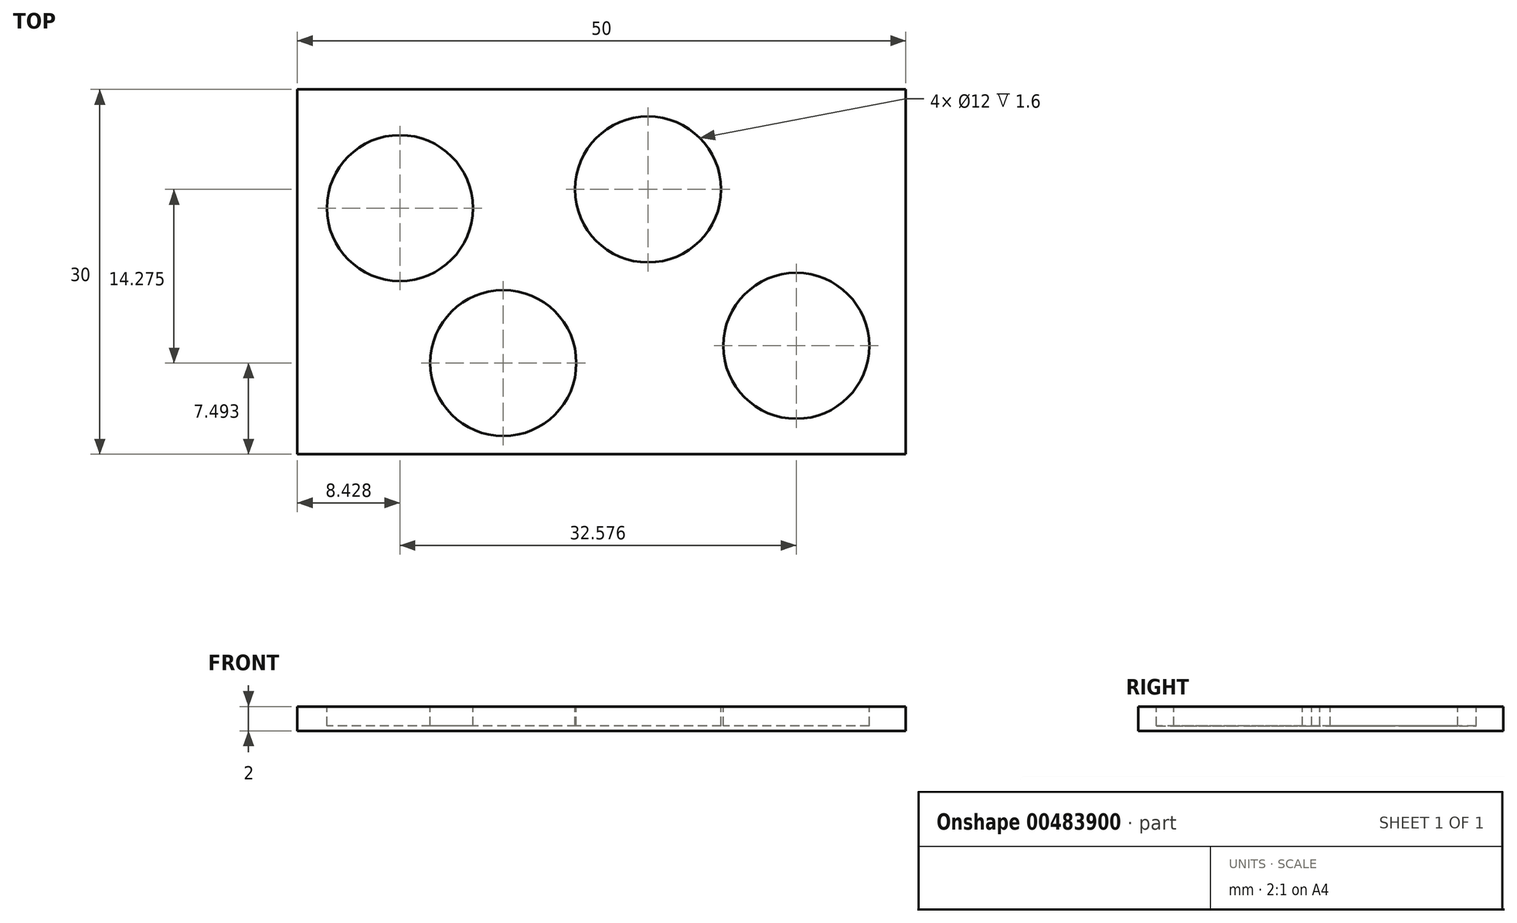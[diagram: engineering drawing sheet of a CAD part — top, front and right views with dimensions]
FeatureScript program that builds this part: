
annotation { "Feature Type Name" : "Feature", "Feature Type Description" : "" }
export const myFeature = defineFeature(function(context is Context, id is Id, definition is map)
    precondition{}
    {
        {
            var Q0;
            Q0=qCreatedBy(makeId("Top.planeOp"),FACE);
            var sketch = newSketch(context, id + "F0", { "sketchPlane" : qUnion([Q0])});
            skLineSegment(sketch, "E0.bottom", {"start": v(-25, 15) * mm, "end": v(25, 15) * mm});
            skLineSegment(sketch, "E0.top", {"start": v(-25, -15) * mm, "end": v(25, -15) * mm});
            skLineSegment(sketch, "E0.left", {"start": v(-25, 15) * mm, "end": v(-25, -15) * mm});
            skLineSegment(sketch, "E0.right", {"start": v(25, 15) * mm, "end": v(25, -15) * mm});
            skPoint(sketch, "E0.middle", {"position": v(0, 0) * mm});
            skSolve(sketch);
        }
        {
            var Q0;
            Q0 = qSketchRegion(id + "F0", true);
            extrude(context, id + "F1", {"entities" : qUnion([Q0]), "oppositeDirection" : true, "depth" : 2 * mm});
        }
        {
            var Q0;
            Q0=qCreatedBy(makeId("Top.planeOp"),FACE);
            var sketch = newSketch(context, id + "F2", { "sketchPlane" : qUnion([Q0])});
            skCircle(sketch, "E1", {"center": v(-16.57, 5.24) * mm, "radius": 6 * mm});
            skCircle(sketch, "E2", {"center": v(-8.07, -7.5) * mm, "radius": 6 * mm});
            skCircle(sketch, "E3", {"center": v(3.82, 6.77) * mm, "radius": 6 * mm});
            skCircle(sketch, "E4", {"center": v(16, -6.1) * mm, "radius": 6 * mm});
            skSolve(sketch);
        }
        {
            var Q0;
            Q0 = qSketchRegion(id + "F2", true);
            extrude(context, id + "F3", {"entities" : qUnion([Q0]), "operationType" : NewBodyOperationType.REMOVE, "oppositeDirection" : true, "depth" : 1.6 * mm});
        }
    });
